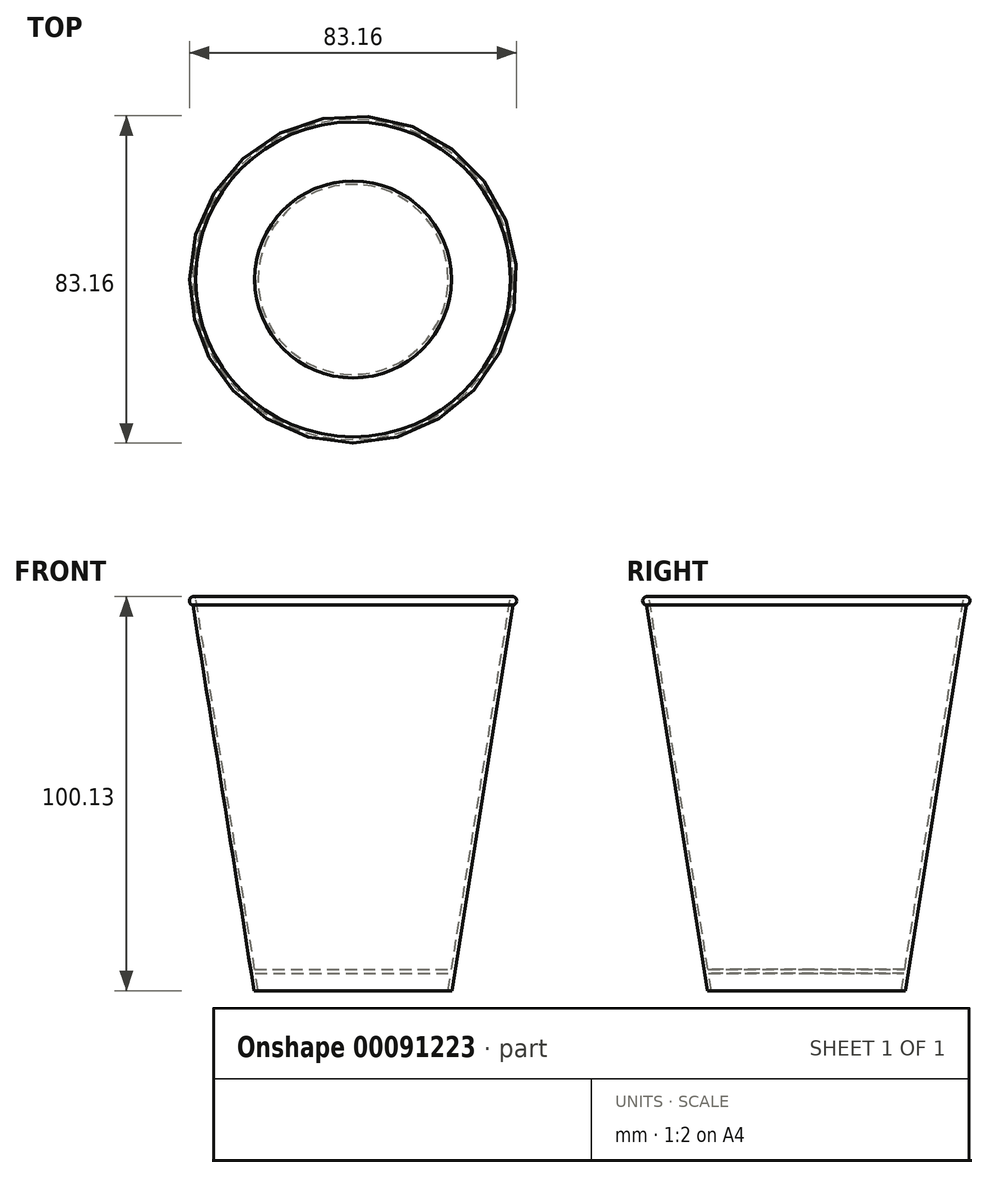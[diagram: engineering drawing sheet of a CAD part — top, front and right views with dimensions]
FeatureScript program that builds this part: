
annotation { "Feature Type Name" : "Feature", "Feature Type Description" : "" }
export const myFeature = defineFeature(function(context is Context, id is Id, definition is map)
    precondition{}
    {
        {
            var Q0;
            Q0=qCreatedBy(makeId("Front.planeOp"),FACE);
            var sketch = newSketch(context, id + "F0", { "sketchPlane" : qUnion([Q0])});
            skLineSegment(sketch, "E0", {"start": v(0, 4.4) * mm, "end": v(24.84, 4.4) * mm});
            skLineSegment(sketch, "E1", {"start": v(0, 4.4) * mm, "end": v(0, 5.4) * mm});
            skLineSegment(sketch, "E2", {"start": v(0, 5.4) * mm, "end": v(25, 5.4) * mm});
            skLineSegment(sketch, "E3", {"start": v(24.14, 0) * mm, "end": v(24.84, 4.4) * mm});
            skLineSegment(sketch, "E4", {"start": v(25.14, 0) * mm, "end": v(40.68, 98) * mm});
            skArc(sketch, "E5", {"start": v(40.68, 98) * mm, "mid": v(41.53, 99.4) * mm, "end": v(40, 100) * mm});
            skLineSegment(sketch, "E6", {"start": v(24.14, 0) * mm, "end": v(25.14, 0) * mm});
            skLineSegment(sketch, "E7.trimOffspring", {"start": v(25, 5.4) * mm, "end": v(40, 100) * mm});
            skSolve(sketch);
        }
        {
            var Q0;
            Q0=makeQuery(id+"F0.imprint","IMPRINT",FACE,{"disambiguationData":[TD([[makeQuery(id+"F0.imprint","IMPRINT",EDGE,{"derivedFrom":sQuery(id+"F0.wireOp",EDGE,"E0")}),1.0]])]});
            var Q1;
            Q1=sQuery(id+"F0.wireOp",EDGE,"E1");
            revolve(context, id + "F1", {"entities" : qUnion([Q0]), "axis" : qUnion([Q1]), "revolveType" : RevolveType.FULL});
        }
    });
